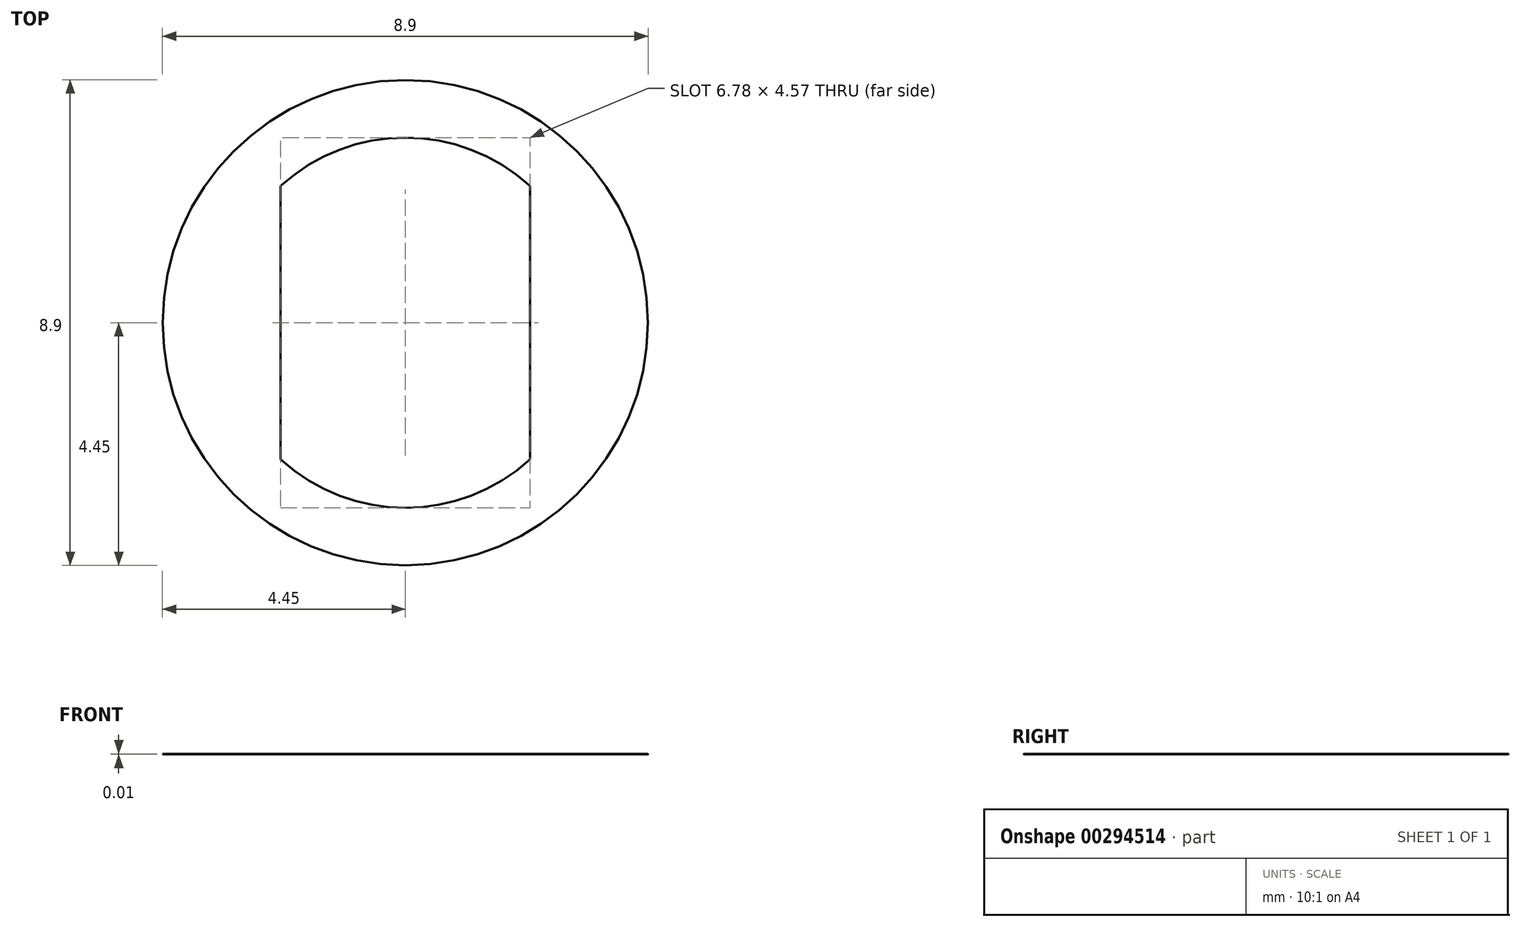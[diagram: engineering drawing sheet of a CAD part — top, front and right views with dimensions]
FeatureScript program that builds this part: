
annotation { "Feature Type Name" : "Feature", "Feature Type Description" : "" }
export const myFeature = defineFeature(function(context is Context, id is Id, definition is map)
    precondition{}
    {
        {
            var Q0;
            Q0=qCreatedBy(makeId("Top.planeOp"),FACE);
            var sketch = newSketch(context, id + "F0", { "sketchPlane" : qUnion([Q0])});
            skCircle(sketch, "E0", {"center": v(0, 0) * mm, "radius": 4.45 * mm});
            skCircle(sketch, "E1", {"center": v(0, 0) * mm, "radius": 3.4 * mm});
            skLineSegment(sketch, "E2", {"start": v(-2.29, 2.5) * mm, "end": v(-2.29, -2.5) * mm});
            skLineSegment(sketch, "E3", {"start": v(2.29, 2.5) * mm, "end": v(2.29, -2.5) * mm});
            skSolve(sketch);
        }
        {
            var Q0;
            Q0=makeQuery(id+"F0.imprint","IMPRINT",FACE,{"disambiguationData":[TD([[makeQuery(id+"F0.imprint","IMPRINT",EDGE,{"derivedFrom":sQuery(id+"F0.wireOp",EDGE,"E0")}),1.0]])]});
            var Q1;
            {var subQ0=sQuery(id+"F0.wireOp",EDGE,"E2");Q1=makeQuery(id+"F0.imprint","IMPRINT",FACE,{"disambiguationData":[TD([[makeQuery(id+"F0.imprint","IMPRINT",EDGE,{"derivedFrom":subQ0}),-1.0]])]});}
            var Q2;
            {var subQ0=sQuery(id+"F0.wireOp",EDGE,"E3");Q2=makeQuery(id+"F0.imprint","IMPRINT",FACE,{"disambiguationData":[TD([[makeQuery(id+"F0.imprint","IMPRINT",EDGE,{"derivedFrom":subQ0}),1.0]])]});}
            extrude(context, id + "F1", {"entities" : qUnion([Q0, Q1, Q2]), "depth" : 3 / 406.4 * mm});
        }
    });
